# Revit family: Two_Handle-Thermostatic_Valve-American_Standard-Townsend-T353.740
name_source: partatom
category: Plumbing Fixtures
revit_build: Autodesk Revit 2018 (Build: 20170223_1515(x64)
units: mm (PartAtom-declared; Revit-internal decimal feet)

## family parameters
Cut with Voids When Loaded = No
Host = Face
OmniClass Number = 23.45.05.14.17
OmniClass Title = Showers
Part Type = Normal
Room Calculation Point = No
Round Connector Dimension = Use Radius
Shared = Yes

## types (1)
- T353.740.002
    ADA Compliant = Yes
    Assembly Code = D2020300
    Bath = No
    CW Connection = Yes
    CWFU = 3
    Cold Water Connection Diameter = 1/2"
    Cold Water Connection Height = 39"
    Cold Water Connection Radius = 1/4"
    Default Elevation = 0"
    Description = Townsend Pressure Balance Bath/Shower Fitting
    Finish = Brass-American Standard-002-Polished Chrome
    HW Connection = Yes
    HWFU = 3
    Height = 74"
    Hot Water Connection Diameter = 1/2"
    Hot Water Connection Height = 39"
    Hot Water Connection Radius = 1/4"
    Length = 9"
    Manufacturer = American Standard
    Material = Brass-American Standard-002-Polished Chrome
    Model = T353.740.002
    NPT Connection Radius = 1/4"
    NPT Connection Size = 1/2"
    Price = Prices may vary. Please consult Manufacturer Representative for most up-to-date price list.
    Product Documentation Link = https://www.americanstandard-us.com
    Product Page URL = https://www.americanstandard-us.com
    Shower = No
    URL = http://www.americanstandard-us.com
    Valve = Yes
    Vent Connection = No
    WFU = 4
    Waste Connection = No
    Width = 7 1/2"

## geometry (parser evidence)
native form markers: Sweep x2
no freeform markers — native parametric forms only
